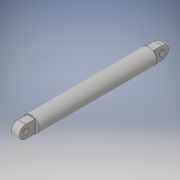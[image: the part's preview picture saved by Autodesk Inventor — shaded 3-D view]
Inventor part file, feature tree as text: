
AUTODESK INVENTOR PART (.ipt)
format: ipt  version: 2016 (Build 200138000, 138)  size: 119,808 bytes
history: native  units: in
note: dims shown in document units (in); Inventor stores cm internally (conversion verified against a paired STEP export)
features: extrude x3, sketch x3, fillet x1, mirror x1
ambient origin geometry x8: Origin, YZ Plane, XZ Plane, XY Plane, X Axis, Y Axis, Z Axis, Center Point
bodies: Solid1 (feature_tree)
feature tree (8):
  extrude  "Extrusion1"  Depth=15.0in TaperAngle=0.0deg
  extrude  "Extrusion4"  Depth=0.8125in
  fillet  "Fillet2"  Radius=2.0in
  extrude  "Extrusion5"  Depth=1.625in
  mirror  "Mirror1"
  sketch  "Sketch1"  dims[d0=2.0in d1=15.0in d2=0.0in]
  sketch  "Sketch4"  dims[d10=2.0in d11=0.0in d12=0.8125in d13=2.0in d14=0.0in]
  sketch  "Sketch5"  dims[d15=1.0in d16=1.625in]
